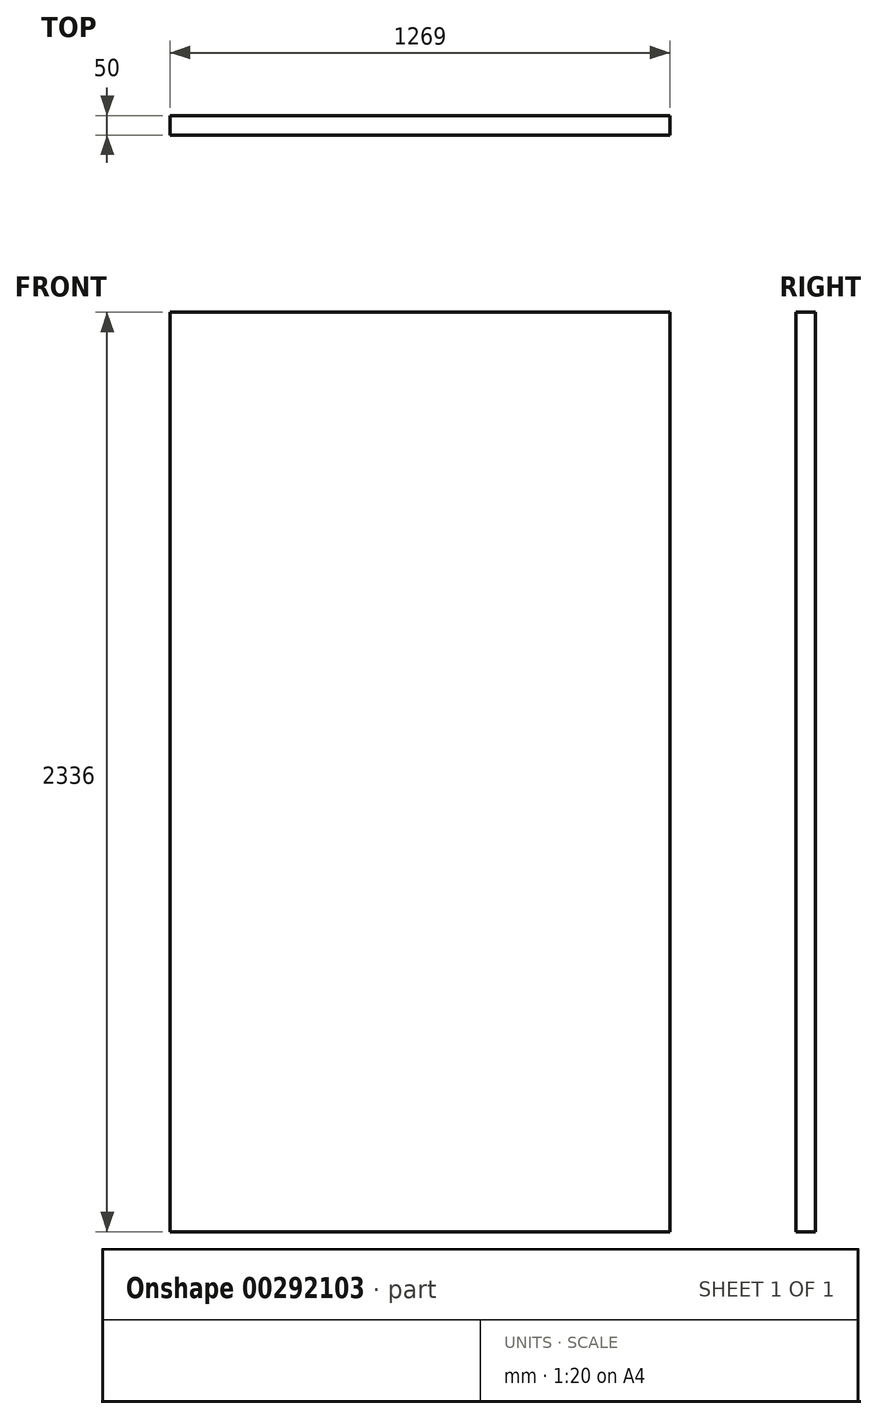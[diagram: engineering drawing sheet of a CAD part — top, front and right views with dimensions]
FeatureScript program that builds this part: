
annotation { "Feature Type Name" : "Feature", "Feature Type Description" : "" }
export const myFeature = defineFeature(function(context is Context, id is Id, definition is map)
    precondition{}
    {
        {
            var Q0;
            Q0=qCreatedBy(makeId("Front.planeOp"),FACE);
            var sketch = newSketch(context, id + "F0", { "sketchPlane" : qUnion([Q0])});
            skLineSegment(sketch, "E0.bottom", {"start": v(634.5, -1168) * mm, "end": v(-634.5, -1168) * mm});
            skLineSegment(sketch, "E0.top", {"start": v(634.5, 1168) * mm, "end": v(-634.5, 1168) * mm});
            skLineSegment(sketch, "E0.left", {"start": v(634.5, -1168) * mm, "end": v(634.5, 1168) * mm});
            skLineSegment(sketch, "E0.right", {"start": v(-634.5, -1168) * mm, "end": v(-634.5, 1168) * mm});
            skPoint(sketch, "E0.middle", {"position": v(0, 0) * mm});
            skSolve(sketch);
        }
        {
            var Q0;
            Q0=makeQuery(id+"F0.imprint","IMPRINT",FACE,{"disambiguationData":[TD([[makeQuery(id+"F0.imprint","IMPRINT",EDGE,{"derivedFrom":sQuery(id+"F0.wireOp",EDGE,"E0.bottom")}),-1.0]])]});
            extrude(context, id + "F1", {"entities" : qUnion([Q0]), "depth" : 50 * mm});
        }
    });
